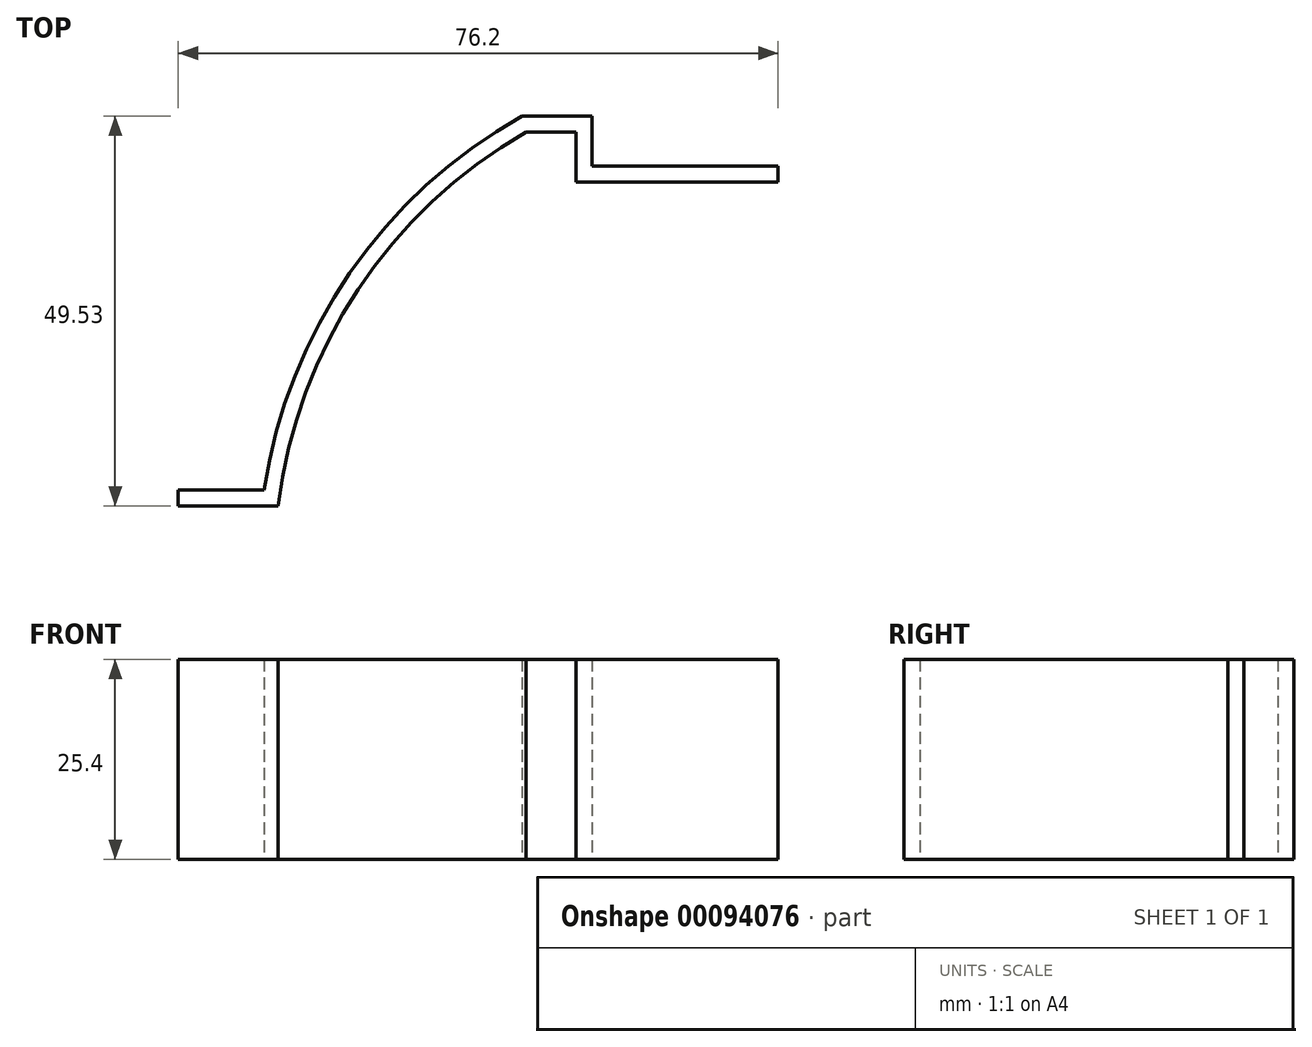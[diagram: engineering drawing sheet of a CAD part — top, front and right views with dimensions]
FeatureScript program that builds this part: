
annotation { "Feature Type Name" : "Feature", "Feature Type Description" : "" }
export const myFeature = defineFeature(function(context is Context, id is Id, definition is map)
    precondition{}
    {
        {
            var Q0;
            Q0=qCreatedBy(makeId("Top.planeOp"),FACE);
            var sketch = newSketch(context, id + "F0", { "sketchPlane" : qUnion([Q0])});
            skLineSegment(sketch, "E0", {"start": v(0, 0) * mm, "end": v(-25.65, 0) * mm});
            skLineSegment(sketch, "E1", {"start": v(-25.65, 0) * mm, "end": v(-25.65, 6.35) * mm});
            skLineSegment(sketch, "E2", {"start": v(-25.65, 6.35) * mm, "end": v(-32, 6.35) * mm});
            skArc(sketch, "E3", {"start": v(-32, 6.35) * mm, "mid": v(-53.38, -13.67) * mm, "end": v(-63.5, -41.15) * mm});
            skLineSegment(sketch, "E4", {"start": v(-63.5, -41.15) * mm, "end": v(-76.2, -41.15) * mm});
            skLineSegment(sketch, "E5", {"start": v(0, 0) * mm, "end": v(0, 2.03) * mm});
            skLineSegment(sketch, "E6", {"start": v(-76.2, -41.15) * mm, "end": v(-76.2, -39.12) * mm});
            skLineSegment(sketch, "E7.0", {"start": v(-65.28, -39.12) * mm, "end": v(-76.2, -39.12) * mm});
            skLineSegment(sketch, "E7.1", {"start": v(0, 2.03) * mm, "end": v(-23.62, 2.03) * mm});
            skLineSegment(sketch, "E7.2", {"start": v(-23.62, 2.03) * mm, "end": v(-23.62, 8.38) * mm});
            skLineSegment(sketch, "E7.3", {"start": v(-23.62, 8.38) * mm, "end": v(-32.54, 8.38) * mm});
            skArc(sketch, "E7.4", {"start": v(-32.54, 8.38) * mm, "mid": v(-54.42, -11.57) * mm, "end": v(-65.28, -39.12) * mm});
            skSolve(sketch);
        }
        {
            var Q0;
            Q0=makeQuery(id+"F0.imprint","IMPRINT",FACE,{"disambiguationData":[TD([[makeQuery(id+"F0.imprint","IMPRINT",EDGE,{"derivedFrom":sQuery(id+"F0.wireOp",EDGE,"E0")}),-1.0]])]});
            extrude(context, id + "F1", {"entities" : qUnion([Q0]), "depth" : 25.4 * mm, "offsetDistance" : 25.4 * mm});
        }
    });
